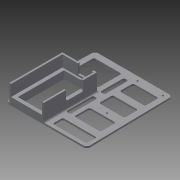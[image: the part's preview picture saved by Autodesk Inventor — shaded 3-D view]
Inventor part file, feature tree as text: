
AUTODESK INVENTOR PART (.ipt)
format: ipt  version: 2014 SP1 (Build 180222100, 222)  size: 269,824 bytes
history: native  units: in
note: dims shown in document units (in); Inventor stores cm internally (conversion verified against a paired STEP export)
features: extrude x9, sketch x7, fillet x2
ambient origin geometry x8: Origin, YZ Plane, XZ Plane, XY Plane, X Axis, Y Axis, Z Axis, Center Point
bodies: Solid1 (feature_tree)
feature tree (18):
  extrude  "Extrusion1"  Depth=0.25in
  fillet  "Fillet1"  Radius=0.12in
  extrude  "Extrusion3"  Depth=6.375in
  extrude  "Extrusion20"  Depth=1.25in TaperAngle=0.0deg
  extrude  "Extrusion21"  Depth=2.52in
  extrude  "Extrusion22"  Depth=3.75in
  extrude  "Extrusion23"  Depth=0.125in
  extrude  "Extrusion24"  Depth=0.125in TaperAngle=0.0deg
  extrude  "Extrusion25"  Depth=0.125in
  fillet  "Fillet8"  Radius=0.125in
  extrude  "Extrusion26"  Depth=0.125in
  sketch  "Sketch3"  dims[d2=0.12in d3=0.0in d4=0.25in d12=0.12in d13=0.0in]
  sketch  "Sketch20"  dims[d60=5.65in d62=6.375in]
  sketch  "Sketch21"  dims[d63=5.9in d98=1.25in d99=0.0in]
  sketch  "Sketch22"  dims[d100=3.875in d101=2.52in]
  sketch  "Sketch23"  dims[d102=2.27in d103=3.75in]
  sketch  "Sketch25"  dims[d104=0.125in d105=0.125in]
  sketch  "Sketch26"  dims[d106=1.0in d107=0.125in d108=0.0in d111=0.125in d112=0.125in d113=0.0in d114=1.77in d115=0.425in d116=0.0in d122=0.12in d123=0.0in d127=0.125in d128=0.125in d129=0.125in d130=1.8594in d131=3.15in d132=0.9297in d133=2.5in d134=0.75in d135=0.125in d139=0.12in d140=0.0in d142=0.125in d146=0.125in d147=0.7in d148=1.25in d149=0.7in d150=2.0in d151=0.0in d152=0.125in d153=0.25in d154=0.125in d155=0.35in d156=0.35in]
